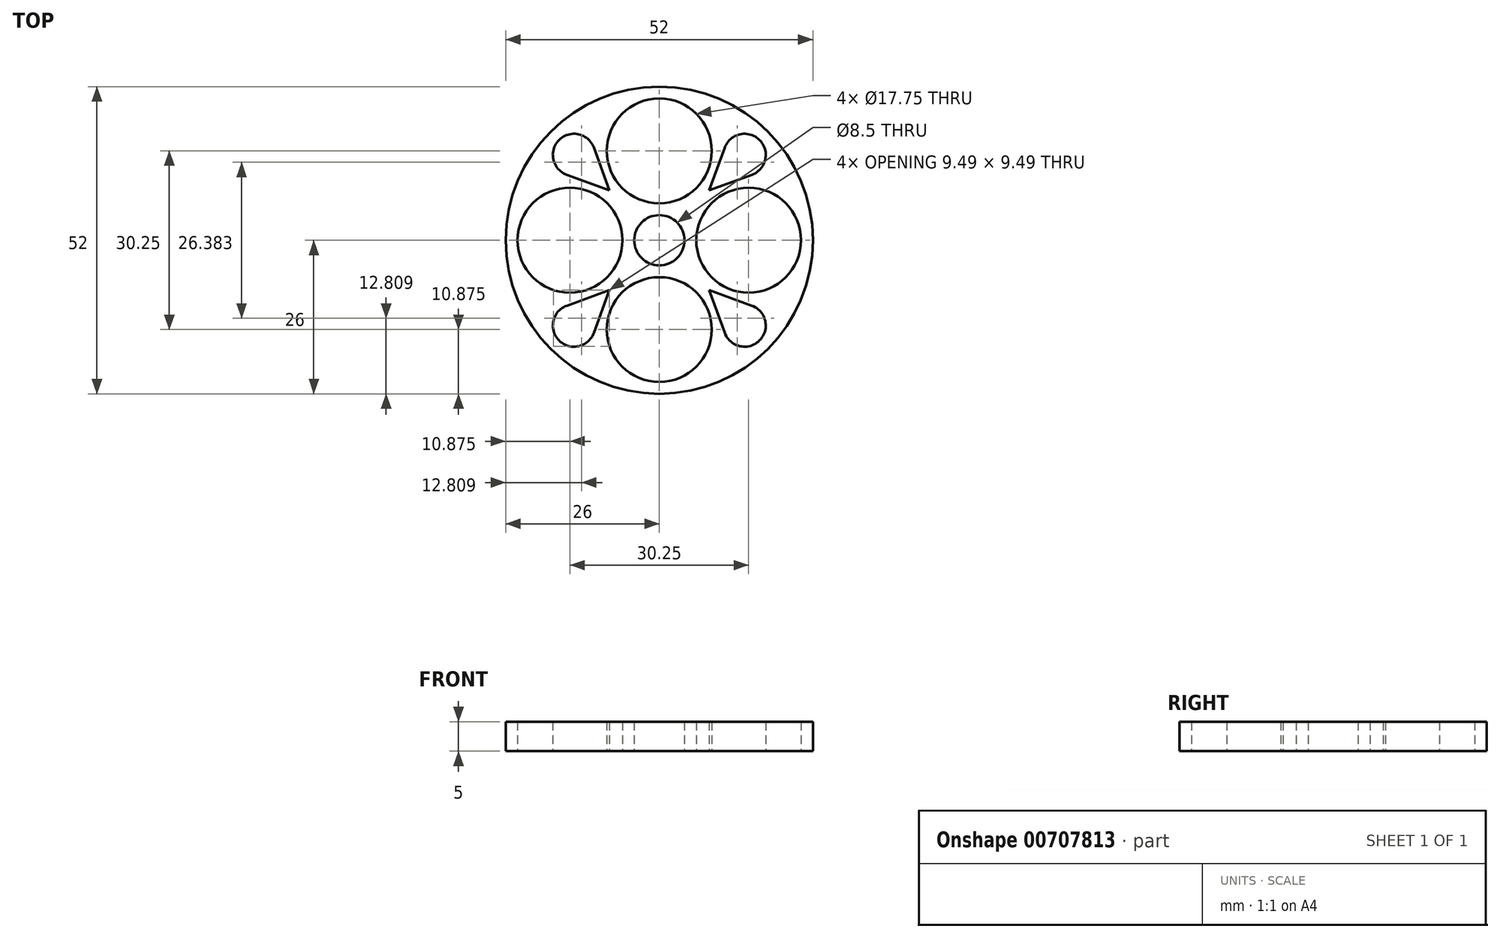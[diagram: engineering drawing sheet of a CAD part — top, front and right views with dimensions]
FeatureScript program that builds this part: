
annotation { "Feature Type Name" : "Feature", "Feature Type Description" : "" }
export const myFeature = defineFeature(function(context is Context, id is Id, definition is map)
    precondition{}
    {
        {
            var Q0;
            Q0=qCreatedBy(makeId("Top.planeOp"),FACE);
            var sketch = newSketch(context, id + "F0", { "sketchPlane" : qUnion([Q0])});
            skCircle(sketch, "E0", {"center": v(0, 0) * mm, "radius": 26 * mm});
            skCircle(sketch, "E1", {"center": v(0, 0) * mm, "radius": 4.25 * mm});
            skCircle(sketch, "E2", {"center": v(0, 15.12) * mm, "radius": 8.88 * mm});
            skLineSegment(sketch, "E3", {"start": v(0, 0) * mm, "end": v(-22.82, 22.82) * mm, "construction": true});
            skLineSegment(sketch, "E4.MirrorCS", {"start": v(0, 0) * mm, "end": v(22.82, 22.82) * mm, "construction": true});
            skLineSegment(sketch, "E5.MirrorCS", {"start": v(0, 0) * mm, "end": v(-22.82, -22.82) * mm, "construction": true});
            skLineSegment(sketch, "E6.MirrorCS", {"start": v(0, 0) * mm, "end": v(22.82, -22.82) * mm, "construction": true});
            skCircle(sketch, "E7.MirrorC", {"center": v(15.12, 0) * mm, "radius": 8.88 * mm});
            skCircle(sketch, "E8.MirrorC", {"center": v(-15.12, 0) * mm, "radius": 8.88 * mm});
            skCircle(sketch, "E9.MirrorC", {"center": v(0, -15.12) * mm, "radius": 8.88 * mm});
            skCircle(sketch, "E10", {"center": v(-14.44, 14.44) * mm, "radius": 3.58 * mm});
            skLineSegment(sketch, "E11", {"start": v(-8.45, 8.45) * mm, "end": v(-15.66, 11.07) * mm});
            skLineSegment(sketch, "E12.MirrorCS", {"start": v(-8.45, 8.45) * mm, "end": v(-11.07, 15.66) * mm});
            skLineSegment(sketch, "E13.MirrorCS", {"start": v(8.45, 8.45) * mm, "end": v(11.07, 15.66) * mm});
            skLineSegment(sketch, "E14.MirrorCS", {"start": v(8.45, 8.45) * mm, "end": v(15.66, 11.07) * mm});
            skCircle(sketch, "E15.MirrorC", {"center": v(14.44, 14.44) * mm, "radius": 3.58 * mm});
            skCircle(sketch, "E16.MirrorC", {"center": v(-14.44, -14.44) * mm, "radius": 3.58 * mm});
            skLineSegment(sketch, "E17.MirrorCS", {"start": v(-8.45, -8.45) * mm, "end": v(-15.66, -11.07) * mm});
            skLineSegment(sketch, "E18.MirrorCS", {"start": v(-8.45, -8.45) * mm, "end": v(-11.07, -15.66) * mm});
            skLineSegment(sketch, "E19.MirrorCS", {"start": v(8.45, -8.45) * mm, "end": v(11.07, -15.66) * mm});
            skLineSegment(sketch, "E20.MirrorCS", {"start": v(8.45, -8.45) * mm, "end": v(15.66, -11.07) * mm});
            skCircle(sketch, "E21.MirrorC", {"center": v(14.44, -14.44) * mm, "radius": 3.58 * mm});
            skSolve(sketch);
        }
        {
            var Q0;
            Q0=makeQuery(id+"F0.imprint","IMPRINT",FACE,{"disambiguationData":[TD([[makeQuery(id+"F0.imprint","IMPRINT",EDGE,{"derivedFrom":sQuery(id+"F0.wireOp",EDGE,"E0")}),1.0]])]});
            extrude(context, id + "F1", {"entities" : qUnion([Q0]), "depth" : 5 * mm, "offsetDistance" : 25 * mm});
        }
    });
